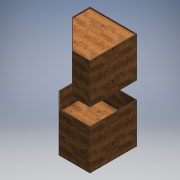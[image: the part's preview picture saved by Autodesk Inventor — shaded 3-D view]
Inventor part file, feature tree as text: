
AUTODESK INVENTOR PART (.ipt)
format: ipt  version: 2016 (Build 200138000, 138)  size: 261,120 bytes
history: native  units: mm
features: extrude x9, sketch x8, plane x4, projected_geometry x4
ambient origin geometry x8: Origin, YZ Plane, XZ Plane, XY Plane, X Axis, Y Axis, Z Axis, Center Point
bodies: Solid1 (feature_tree)
feature tree (25):
  extrude  "Extrusion1"  Depth=350.0mm
  plane  "Work Plane1"
  extrude  "Extrusion2"  Depth=80.0mm
  extrude  "Extrusion3"  TaperAngle=0.0deg  [1 undecoded]
  plane  "Work Plane2"
  extrude  "Extrusion8"  Depth=30.0mm
  extrude  "Extrusion9"  TaperAngle=0.0deg  [1 undecoded]
  extrude  "Extrusion10"  Depth=400.0mm
  extrude  "Extrusion11"  TaperAngle=0.0deg  [1 undecoded]
  plane  "Work Plane3"
  plane  "Work Plane4"
  extrude  "Extrusion12"  TaperAngle=0.0deg  [1 undecoded]
  extrude  "Extrusion13"  Depth=30.0mm
  sketch  "Sketch2"  dims[d6=45.0deg d8=350.0mm]
  sketch  "Sketch4"  dims[d10=0.0mm d11=80.0mm]
  projected_geometry  "Projected Loop1"
  sketch  "Sketch5"  dims[d12=10.0mm d14=0.0mm]
  sketch  "Sketch12"  dims[d15=30.0mm d16=30.0mm]
  sketch  "Sketch13"  dims[d17=30.0mm d18=0.0mm]
  projected_geometry  "Projected Loop3"
  sketch  "Sketch14"  dims[d19=1000.0mm d20=0.0mm d32=400.0mm]
  sketch  "Sketch15"  dims[d33=10.0mm d34=0.0mm]
  projected_geometry  "Projected Loop4"
  sketch  "Sketch17"  dims[d35=10.0mm d37=0.0mm d38=30.0mm d39=750.0mm d40=0.0mm d41=10.0mm d42=0.0mm d43=375.0mm d44=400.0mm d45=10.0mm d46=0.0mm d47=10.0mm d48=0.0mm]
  projected_geometry  "Projected Loop5"
note: 4 required parameter values undecoded (feature->parameter linkage not recoverable at this tier; creation-order binding heuristic only, values carry confidence <= 0.55)
